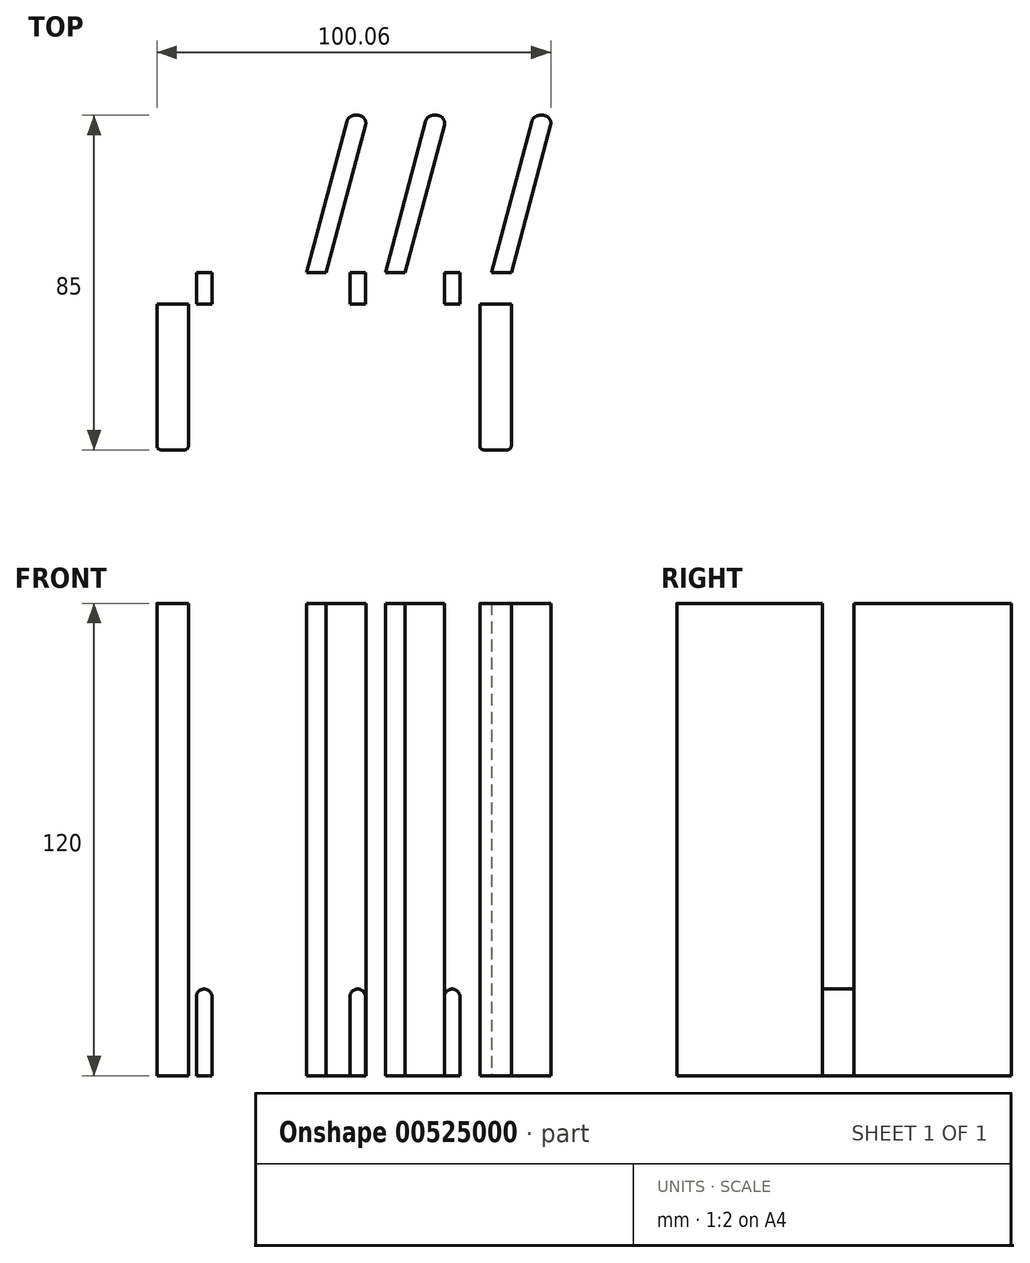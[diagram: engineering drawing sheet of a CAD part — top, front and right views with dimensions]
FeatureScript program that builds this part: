
annotation { "Feature Type Name" : "Feature", "Feature Type Description" : "" }
export const myFeature = defineFeature(function(context is Context, id is Id, definition is map)
    precondition{}
    {
        {
            var Q0;
            Q0=qCreatedBy(makeId("Top.planeOp"),FACE);
            var sketch = newSketch(context, id + "F0", { "sketchPlane" : qUnion([Q0])});
            skLineSegment(sketch, "E0.bottom", {"start": v(45, 22.5) * mm, "end": v(-45, 22.5) * mm});
            skLineSegment(sketch, "E0.top", {"start": v(45, -22.5) * mm, "end": v(-45, -22.5) * mm});
            skLineSegment(sketch, "E0.left", {"start": v(45, 22.5) * mm, "end": v(45, -22.5) * mm});
            skLineSegment(sketch, "E0.right", {"start": v(-45, 22.5) * mm, "end": v(-45, -22.5) * mm});
            skPoint(sketch, "E0.middle", {"position": v(0, 0) * mm});
            skSolve(sketch);
        }
        {
            var Q0;
            Q0=makeQuery(id+"F0.imprint","IMPRINT",FACE,{"disambiguationData":[TD([[makeQuery(id+"F0.imprint","IMPRINT",EDGE,{"derivedFrom":sQuery(id+"F0.wireOp",EDGE,"E0.bottom")}),1.0]])]});
            extrude(context, id + "F1", {"entities" : qUnion([Q0]), "depth" : 120 * mm, "offsetDistance" : 25 * mm});
        }
        {
            var Q0;
            Q0=makeQuery(id+"F1.opExtrude","CAP_FACE",FACE,{"disambiguationData":[OSD([sQuery(id+"F0.wireOp",EDGE,"E0.bottom"),sQuery(id+"F0.wireOp",EDGE,"E0.top"),sQuery(id+"F0.wireOp",EDGE,"E0.left"),sQuery(id+"F0.wireOp",EDGE,"E0.right")])],"isStart":false});
            var Q1;
            Q1=makeQuery(id+"F1.opExtrude","SWEPT_FACE",FACE,{"disambiguationData":[OSD([sQuery(id+"F0.wireOp",EDGE,"E0.top")])]});
            var Q2;
            Q2=makeQuery(id+"F1.opExtrude","CAP_FACE",FACE,{"disambiguationData":[OSD([sQuery(id+"F0.wireOp",EDGE,"E0.bottom"),sQuery(id+"F0.wireOp",EDGE,"E0.top"),sQuery(id+"F0.wireOp",EDGE,"E0.left"),sQuery(id+"F0.wireOp",EDGE,"E0.right")])],"isStart":true});
            shell(context, id + "F2", {"entities" : qUnion([Q0, Q1, Q2]), "thickness" : 8 * mm});
        }
        {
            var Q0;
            {var subQ1=sQuery(id+"F5.wireOp",EDGE,"E24.2.0.0");var subQ5=sQuery(id+"F0.wireOp",EDGE,"E0.bottom");Q0=makeQuery(id+"F6.boolean.opBoolean","SPLIT",FACE,{"disambiguationData":[TD([makeQuery(id+"F6.opExtrude","SWEPT_FACE",FACE,{"disambiguationData":[OSD([subQ1])]})])],"derivedFrom":makeQuery(id+"F1.opExtrude","SWEPT_FACE",FACE,{"disambiguationData":[OSD([subQ5])]})});}
            var sketch = newSketch(context, id + "F3", { "sketchPlane" : qUnion([Q0])});
            skLineSegment(sketch, "E1.bottom", {"start": v(-32, 120) * mm, "end": v(-28, 120) * mm});
            skLineSegment(sketch, "E1.left", {"start": v(-32, 120) * mm, "end": v(-32, 100) * mm});
            skLineSegment(sketch, "E1.right", {"start": v(-28, 120) * mm, "end": v(-28, 100) * mm});
            skArc(sketch, "E2", {"start": v(-32, 100) * mm, "mid": v(-30, 98) * mm, "end": v(-28, 100) * mm});
            skLineSegment(sketch, "E3", {"start": v(-45, 60) * mm, "end": v(45, 60) * mm, "construction": true});
            skLineSegment(sketch, "E4.1.0.0", {"start": v(-8, 120) * mm, "end": v(-8, 100) * mm});
            skLineSegment(sketch, "E4.1.0.1", {"start": v(-4, 120) * mm, "end": v(-4, 100) * mm});
            skArc(sketch, "E4.1.0.2", {"start": v(-8, 100) * mm, "mid": v(-6, 98) * mm, "end": v(-4, 100) * mm});
            skLineSegment(sketch, "E4.1.0.3", {"start": v(-8, 120) * mm, "end": v(-4, 120) * mm});
            skLineSegment(sketch, "E4.2.0.0", {"start": v(12, 120) * mm, "end": v(12, 100) * mm});
            skLineSegment(sketch, "E4.2.0.1", {"start": v(16, 120) * mm, "end": v(16, 100) * mm});
            skArc(sketch, "E4.2.0.2", {"start": v(12, 100) * mm, "mid": v(14, 98) * mm, "end": v(16, 100) * mm});
            skLineSegment(sketch, "E4.2.0.3", {"start": v(12, 120) * mm, "end": v(16, 120) * mm});
            skLineSegment(sketch, "E5.0.3.0", {"start": v(31, 120) * mm, "end": v(31, 100) * mm});
            skLineSegment(sketch, "E5.3.3.0", {"start": v(35, 120) * mm, "end": v(35, 100) * mm});
            skArc(sketch, "E5.6.3.0", {"start": v(31, 100) * mm, "mid": v(33, 98) * mm, "end": v(35, 100) * mm});
            skLineSegment(sketch, "E5.10.3.0", {"start": v(31, 120) * mm, "end": v(35, 120) * mm});
            skArc(sketch, "E6.MirrorCS", {"start": v(-32, 20) * mm, "mid": v(-30, 22) * mm, "end": v(-28, 20) * mm});
            skArc(sketch, "E7.MirrorCS", {"start": v(-8, 20) * mm, "mid": v(-6, 22) * mm, "end": v(-4, 20) * mm});
            skLineSegment(sketch, "E8.MirrorCS", {"start": v(-32, 0) * mm, "end": v(-28, 0) * mm});
            skLineSegment(sketch, "E9.MirrorCS", {"start": v(12, 0) * mm, "end": v(16, 0) * mm});
            skArc(sketch, "E10.MirrorCS", {"start": v(31, 20) * mm, "mid": v(33, 22) * mm, "end": v(35, 20) * mm});
            skLineSegment(sketch, "E11.MirrorCS", {"start": v(31, 0) * mm, "end": v(35, 0) * mm});
            skArc(sketch, "E12.MirrorCS", {"start": v(12, 20) * mm, "mid": v(14, 22) * mm, "end": v(16, 20) * mm});
            skLineSegment(sketch, "E13.MirrorCS", {"start": v(-8, 0) * mm, "end": v(-4, 0) * mm});
            skLineSegment(sketch, "E14.MirrorCS", {"start": v(-28, 0) * mm, "end": v(-28, 20) * mm});
            skLineSegment(sketch, "E15.MirrorCS", {"start": v(31, 0) * mm, "end": v(31, 20) * mm});
            skLineSegment(sketch, "E16.MirrorCS", {"start": v(-8, 0) * mm, "end": v(-8, 20) * mm});
            skLineSegment(sketch, "E17.MirrorCS", {"start": v(16, 0) * mm, "end": v(16, 20) * mm});
            skLineSegment(sketch, "E18.MirrorCS", {"start": v(35, 0) * mm, "end": v(35, 20) * mm});
            skLineSegment(sketch, "E19.MirrorCS", {"start": v(-32, 0) * mm, "end": v(-32, 20) * mm});
            skLineSegment(sketch, "E20.MirrorCS", {"start": v(-4, 0) * mm, "end": v(-4, 20) * mm});
            skLineSegment(sketch, "E21.MirrorCS", {"start": v(12, 0) * mm, "end": v(12, 20) * mm});
            skSolve(sketch);
        }
        {
            var Q0;
            Q0=makeQuery(id+"F3.imprint","IMPRINT",FACE,{"disambiguationData":[TD([[makeQuery(id+"F3.imprint","IMPRINT",EDGE,{"derivedFrom":sQuery(id+"F3.wireOp",EDGE,"E6.MirrorCS")}),-1.0]])]});
            var Q1;
            Q1=makeQuery(id+"F3.imprint","IMPRINT",FACE,{"disambiguationData":[TD([[makeQuery(id+"F3.imprint","IMPRINT",EDGE,{"derivedFrom":sQuery(id+"F3.wireOp",EDGE,"E7.MirrorCS")}),-1.0]])]});
            var Q2;
            Q2=makeQuery(id+"F3.imprint","IMPRINT",FACE,{"disambiguationData":[TD([[makeQuery(id+"F3.imprint","IMPRINT",EDGE,{"derivedFrom":sQuery(id+"F3.wireOp",EDGE,"E9.MirrorCS")}),1.0]])]});
            var Q3;
            Q3=makeQuery(id+"F3.imprint","IMPRINT",FACE,{"disambiguationData":[TD([[makeQuery(id+"F3.imprint","IMPRINT",EDGE,{"derivedFrom":sQuery(id+"F3.wireOp",EDGE,"E10.MirrorCS")}),-1.0]])]});
            var Q4;
            Q4=makeQuery(id+"F3.imprint","IMPRINT",FACE,{"disambiguationData":[TD([[makeQuery(id+"F3.imprint","IMPRINT",EDGE,{"derivedFrom":sQuery(id+"F3.wireOp",EDGE,"E5.0.3.0")}),1.0]])]});
            var Q5;
            Q5=makeQuery(id+"F3.imprint","IMPRINT",FACE,{"disambiguationData":[TD([[makeQuery(id+"F3.imprint","IMPRINT",EDGE,{"derivedFrom":sQuery(id+"F3.wireOp",EDGE,"E4.2.0.0")}),1.0]])]});
            var Q6;
            Q6=makeQuery(id+"F3.imprint","IMPRINT",FACE,{"disambiguationData":[TD([[makeQuery(id+"F3.imprint","IMPRINT",EDGE,{"derivedFrom":sQuery(id+"F3.wireOp",EDGE,"E4.1.0.0")}),1.0]])]});
            var Q7;
            Q7=makeQuery(id+"F3.imprint","IMPRINT",FACE,{"disambiguationData":[TD([[makeQuery(id+"F3.imprint","IMPRINT",EDGE,{"derivedFrom":sQuery(id+"F3.wireOp",EDGE,"E1.bottom")}),-1.0]])]});
            var Q8;
            Q8=makeQuery(id+"F2.opShell","OFFSET_FACE",FACE,{"disambiguationData":[OSD([sQuery(id+"F0.wireOp",EDGE,"E0.bottom")])]});
            extrude(context, id + "F4", {"entities" : qUnion([Q0, Q1, Q2, Q3, Q4, Q5, Q6, Q7]), "operationType" : NewBodyOperationType.REMOVE, "endBound" : BoundingType.UP_TO_SURFACE, "oppositeDirection" : true, "depth" : 25 * mm, "endBoundEntityFace" : qUnion([Q8]), "offsetDistance" : 25 * mm});
        }
        {
            var Q0;
            Q0=makeQuery(id+"F1.opExtrude","CAP_FACE",FACE,{"disambiguationData":[OSD([sQuery(id+"F0.wireOp",EDGE,"E0.bottom"),sQuery(id+"F0.wireOp",EDGE,"E0.top"),sQuery(id+"F0.wireOp",EDGE,"E0.left"),sQuery(id+"F0.wireOp",EDGE,"E0.right")])],"isStart":true});
            var sketch = newSketch(context, id + "F5", { "sketchPlane" : qUnion([Q0])});
            skLineSegment(sketch, "E22.bottom", {"start": v(-45, -22.5) * mm, "end": v(-40, -22.5) * mm});
            skLineSegment(sketch, "E22.top", {"start": v(-41, -37.5) * mm, "end": v(-36, -37.5) * mm});
            skLineSegment(sketch, "E22.left", {"start": v(-45, -22.5) * mm, "end": v(-41, -37.5) * mm});
            skLineSegment(sketch, "E22.right", {"start": v(-40, -22.5) * mm, "end": v(-36, -37.5) * mm});
            skLineSegment(sketch, "E23.bottom", {"start": v(-27, -22.5) * mm, "end": v(-22, -22.5) * mm});
            skLineSegment(sketch, "E23.top", {"start": v(-16.33, -62.5) * mm, "end": v(-11.33, -62.5) * mm});
            skLineSegment(sketch, "E23.left", {"start": v(-27, -22.5) * mm, "end": v(-16.33, -62.5) * mm});
            skLineSegment(sketch, "E23.right", {"start": v(-22, -22.5) * mm, "end": v(-11.33, -62.5) * mm});
            skLineSegment(sketch, "E24.1.0.0", {"start": v(-2, -22.5) * mm, "end": v(8.67, -62.5) * mm});
            skLineSegment(sketch, "E24.1.0.1", {"start": v(-7, -22.5) * mm, "end": v(3.67, -62.5) * mm});
            skLineSegment(sketch, "E24.1.0.2", {"start": v(-7, -22.5) * mm, "end": v(-2, -22.5) * mm});
            skLineSegment(sketch, "E24.1.0.3", {"start": v(3.67, -62.5) * mm, "end": v(8.67, -62.5) * mm});
            skLineSegment(sketch, "E24.2.0.0", {"start": v(18, -22.5) * mm, "end": v(28.67, -62.5) * mm});
            skLineSegment(sketch, "E24.2.0.1", {"start": v(13, -22.5) * mm, "end": v(23.67, -62.5) * mm});
            skLineSegment(sketch, "E24.2.0.2", {"start": v(13, -22.5) * mm, "end": v(18, -22.5) * mm});
            skLineSegment(sketch, "E24.2.0.3", {"start": v(23.67, -62.5) * mm, "end": v(28.67, -62.5) * mm});
            skLineSegment(sketch, "E24.direction1", {"start": v(-16.33, -62.5) * mm, "end": v(3.67, -62.5) * mm, "construction": true});
            skLineSegment(sketch, "E25", {"start": v(38, -22.5) * mm, "end": v(45, -22.5) * mm});
            skLineSegment(sketch, "E26.1.0.0", {"start": v(40, -22.5) * mm, "end": v(50.67, -62.5) * mm});
            skLineSegment(sketch, "E26.1.0.1", {"start": v(45, -22.5) * mm, "end": v(55.67, -62.5) * mm});
            skLineSegment(sketch, "E26.1.0.2", {"start": v(50.67, -62.5) * mm, "end": v(55.67, -62.5) * mm});
            skLineSegment(sketch, "E26.1.0.3", {"start": v(40, -22.5) * mm, "end": v(45, -22.5) * mm});
            skLineSegment(sketch, "E26.direction1", {"start": v(23.67, -62.5) * mm, "end": v(50.67, -62.5) * mm, "construction": true});
            skSolve(sketch);
        }
        {
            var Q0;
            Q0=makeQuery(id+"F5.imprint","IMPRINT",FACE,{"disambiguationData":[TD([[makeQuery(id+"F5.imprint","IMPRINT",EDGE,{"derivedFrom":sQuery(id+"F5.wireOp",EDGE,"E22.bottom")}),1.0]])]});
            var Q1;
            Q1=makeQuery(id+"F5.imprint","IMPRINT",FACE,{"disambiguationData":[TD([[makeQuery(id+"F5.imprint","IMPRINT",EDGE,{"derivedFrom":sQuery(id+"F5.wireOp",EDGE,"E23.bottom")}),1.0]])]});
            var Q2;
            Q2=makeQuery(id+"F5.imprint","IMPRINT",FACE,{"disambiguationData":[TD([[makeQuery(id+"F5.imprint","IMPRINT",EDGE,{"derivedFrom":sQuery(id+"F5.wireOp",EDGE,"E24.1.0.0")}),-1.0]])]});
            var Q3;
            Q3=makeQuery(id+"F5.imprint","IMPRINT",FACE,{"disambiguationData":[TD([[makeQuery(id+"F5.imprint","IMPRINT",EDGE,{"derivedFrom":sQuery(id+"F5.wireOp",EDGE,"E24.2.0.0")}),-1.0]])]});
            var Q4;
            Q4=makeQuery(id+"F5.imprint","IMPRINT",FACE,{"disambiguationData":[TD([[makeQuery(id+"F5.imprint","IMPRINT",EDGE,{"derivedFrom":sQuery(id+"F5.wireOp",EDGE,"61188b05-475f-47d3-8e35-6b128a10a680.0.3.0")}),-1.0]])]});
            var Q5;
            Q5=makeQuery(id+"F5.imprint","IMPRINT",FACE,{"disambiguationData":[TD([[makeQuery(id+"F5.imprint","IMPRINT",EDGE,{"derivedFrom":sQuery(id+"F5.wireOp",EDGE,"E26.1.0.0")}),1.0]])]});
            var Q6;
            Q6=makeQuery(id+"F1.opExtrude","CAP_FACE",FACE,{"disambiguationData":[OSD([sQuery(id+"F0.wireOp",EDGE,"E0.bottom"),sQuery(id+"F0.wireOp",EDGE,"E0.top"),sQuery(id+"F0.wireOp",EDGE,"E0.left"),sQuery(id+"F0.wireOp",EDGE,"E0.right")])],"isStart":false});
            extrude(context, id + "F6", {"entities" : qUnion([Q0, Q1, Q2, Q3, Q4, Q5]), "operationType" : NewBodyOperationType.ADD, "endBound" : BoundingType.UP_TO_SURFACE, "oppositeDirection" : true, "depth" : 25 * mm, "endBoundEntityFace" : qUnion([Q6]), "offsetDistance" : 25 * mm});
        }
        {
            var Q0;
            Q0=makeQuery(id+"F6.opExtrude","SWEPT_EDGE",EDGE,{"disambiguationData":[OSD([sQuery(id+"F5.wireOp",EDGE,"E26.1.0.1"),sQuery(id+"F5.wireOp",EDGE,"E26.1.0.2")])]});
            var Q1;
            Q1=makeQuery(id+"F6.opExtrude","SWEPT_EDGE",EDGE,{"disambiguationData":[OSD([sQuery(id+"F5.wireOp",EDGE,"E26.1.0.0"),sQuery(id+"F5.wireOp",EDGE,"E26.1.0.2")])]});
            var Q2;
            Q2=makeQuery(id+"F6.opExtrude","SWEPT_EDGE",EDGE,{"disambiguationData":[OSD([sQuery(id+"F5.wireOp",EDGE,"E23.top"),sQuery(id+"F5.wireOp",EDGE,"E23.left")])]});
            var Q3;
            Q3=makeQuery(id+"F6.opExtrude","SWEPT_EDGE",EDGE,{"disambiguationData":[OSD([sQuery(id+"F5.wireOp",EDGE,"E24.1.0.1"),sQuery(id+"F5.wireOp",EDGE,"E24.1.0.3")])]});
            var Q4;
            Q4=makeQuery(id+"F6.opExtrude","SWEPT_EDGE",EDGE,{"disambiguationData":[OSD([sQuery(id+"F5.wireOp",EDGE,"E23.top"),sQuery(id+"F5.wireOp",EDGE,"E23.right")])]});
            var Q5;
            Q5=makeQuery(id+"F6.opExtrude","SWEPT_EDGE",EDGE,{"disambiguationData":[OSD([sQuery(id+"F5.wireOp",EDGE,"E22.top"),sQuery(id+"F5.wireOp",EDGE,"E22.right")])]});
            var Q6;
            Q6=makeQuery(id+"F6.opExtrude","SWEPT_EDGE",EDGE,{"disambiguationData":[OSD([sQuery(id+"F5.wireOp",EDGE,"E22.top"),sQuery(id+"F5.wireOp",EDGE,"E22.left")])]});
            var Q7;
            Q7=makeQuery(id+"F6.opExtrude","SWEPT_EDGE",EDGE,{"disambiguationData":[OSD([sQuery(id+"F5.wireOp",EDGE,"E24.2.0.1"),sQuery(id+"F5.wireOp",EDGE,"E24.2.0.3")])]});
            var Q8;
            Q8=makeQuery(id+"F6.opExtrude","SWEPT_EDGE",EDGE,{"disambiguationData":[OSD([sQuery(id+"F5.wireOp",EDGE,"E24.2.0.0"),sQuery(id+"F5.wireOp",EDGE,"E24.2.0.3")])]});
            var Q9;
            Q9=makeQuery(id+"F6.opExtrude","SWEPT_EDGE",EDGE,{"disambiguationData":[OSD([sQuery(id+"F5.wireOp",EDGE,"E24.1.0.0"),sQuery(id+"F5.wireOp",EDGE,"E24.1.0.3")])]});
            fillet(context, id + "F7", {"entities" : qUnion([Q0, Q1, Q2, Q3, Q4, Q5, Q6, Q7, Q8, Q9]), "radius" : 2 * mm, "tangentPropagation" : true, "allowEdgeOverflow" : false});
        }
        {
            var Q0;
            Q0=makeQuery(id+"F1.opExtrude","SWEPT_EDGE",EDGE,{"disambiguationData":[OSD([sQuery(id+"F0.wireOp",EDGE,"E0.top"),sQuery(id+"F0.wireOp",EDGE,"E0.right")])]});
            var Q1;
            Q1=makeQuery(id+"F2.opShell","OFFSET_EDGE",EDGE,{"disambiguationData":[OSD([sQuery(id+"F0.wireOp",EDGE,"E0.top"),sQuery(id+"F0.wireOp",EDGE,"E0.right")])]});
            var Q2;
            Q2=makeQuery(id+"F2.opShell","OFFSET_EDGE",EDGE,{"disambiguationData":[OSD([sQuery(id+"F0.wireOp",EDGE,"E0.top"),sQuery(id+"F0.wireOp",EDGE,"E0.left")])]});
            var Q3;
            Q3=makeQuery(id+"F1.opExtrude","SWEPT_EDGE",EDGE,{"disambiguationData":[OSD([sQuery(id+"F0.wireOp",EDGE,"E0.top"),sQuery(id+"F0.wireOp",EDGE,"E0.left")])]});
            fillet(context, id + "F8", {"entities" : qUnion([Q0, Q1, Q2, Q3]), "radius" : 1 * mm, "tangentPropagation" : true, "allowEdgeOverflow" : false});
        }
    });
